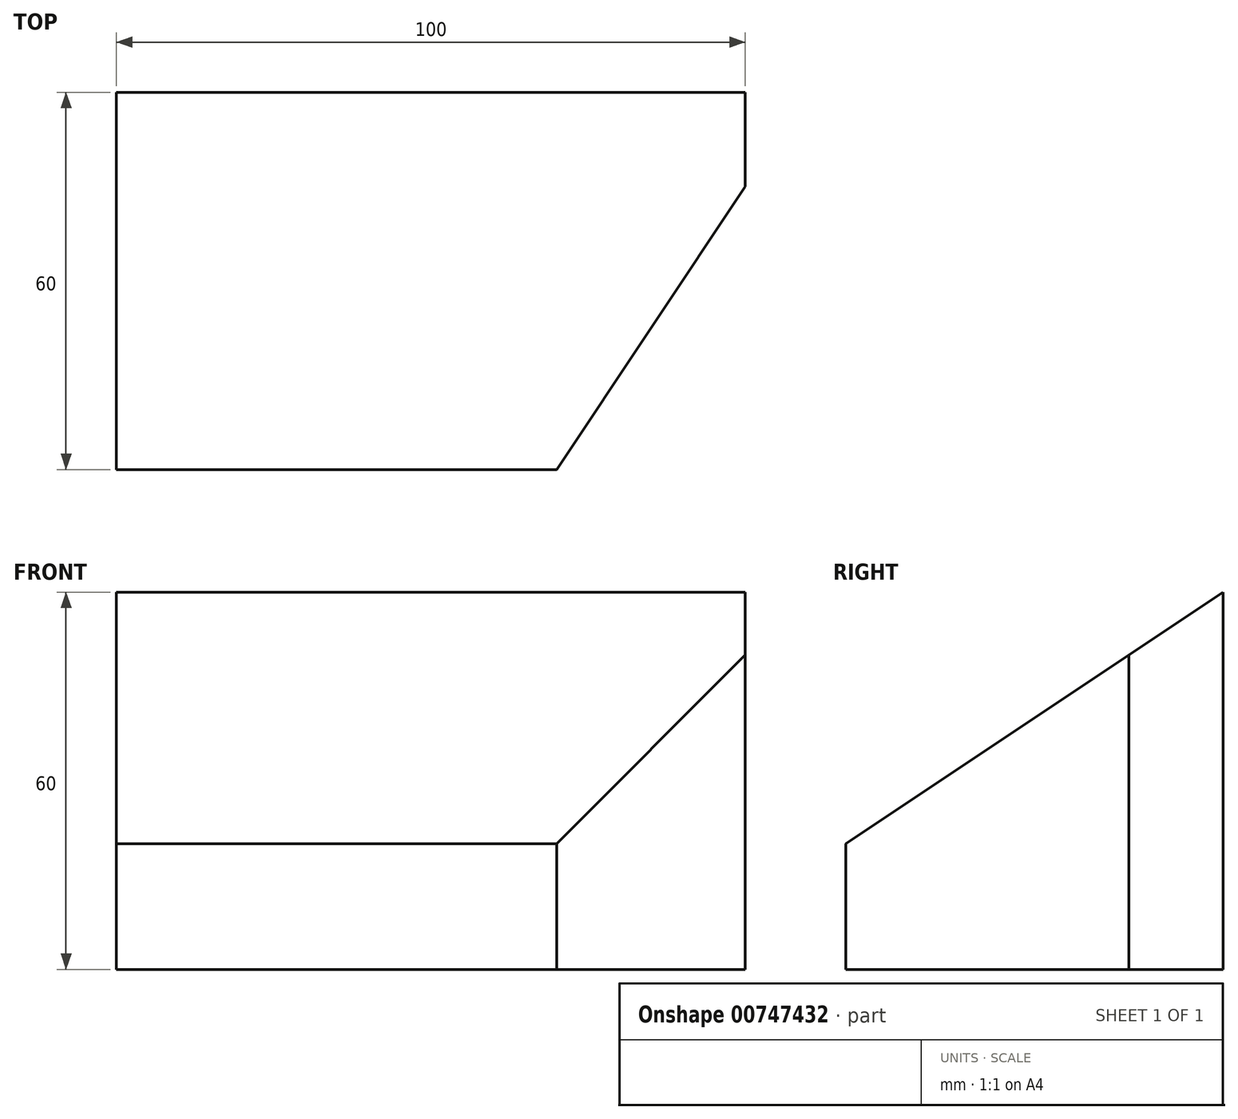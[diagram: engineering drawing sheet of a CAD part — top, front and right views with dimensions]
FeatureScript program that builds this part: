
annotation { "Feature Type Name" : "Feature", "Feature Type Description" : "" }
export const myFeature = defineFeature(function(context is Context, id is Id, definition is map)
    precondition{}
    {
        {
            var Q0;
            Q0=qCreatedBy(makeId("Front.planeOp"),FACE);
            var sketch = newSketch(context, id + "F0", { "sketchPlane" : qUnion([Q0])});
            skLineSegment(sketch, "E0.bottom", {"start": v(0, 0) * mm, "end": v(100, 0) * mm});
            skLineSegment(sketch, "E0.top", {"start": v(0, 60) * mm, "end": v(100, 60) * mm});
            skLineSegment(sketch, "E0.left", {"start": v(0, 0) * mm, "end": v(0, 60) * mm});
            skLineSegment(sketch, "E0.right", {"start": v(100, 0) * mm, "end": v(100, 60) * mm});
            skSolve(sketch);
        }
        {
            var Q0;
            Q0 = qSketchRegion(id + "F0", true);
            extrude(context, id + "F1", {"entities" : qUnion([Q0]), "depth" : 60 * mm, "offsetDistance" : 25 * mm});
        }
        {
            var Q0;
            Q0=makeQuery(id+"F1.opExtrude","SWEPT_FACE",FACE,{"disambiguationData":[OSD([sQuery(id+"F0.wireOp",EDGE,"E0.top")])]});
            var sketch = newSketch(context, id + "F2", { "sketchPlane" : qUnion([Q0])});
            skLineSegment(sketch, "E1", {"start": v(70, -60) * mm, "end": v(100, -15) * mm});
            skSolve(sketch);
        }
        {
            var Q0;
            {var subQ0=sQuery(id+"F2.wireOp",EDGE,"E1");Q0=makeQuery(id+"F2.imprint","IMPRINT",FACE,{"disambiguationData":[TD([[makeQuery(id+"F2.imprint","IMPRINT",EDGE,{"derivedFrom":subQ0}),-1.0]])]});}
            extrude(context, id + "F3", {"entities" : qUnion([Q0]), "operationType" : NewBodyOperationType.REMOVE, "endBound" : BoundingType.THROUGH_ALL, "oppositeDirection" : true, "depth" : 25 * mm, "offsetDistance" : 25 * mm});
        }
        {
            var Q0;
            Q0=makeQuery(id+"F1.opExtrude","SWEPT_FACE",FACE,{"disambiguationData":[OSD([sQuery(id+"F0.wireOp",EDGE,"E0.left")])]});
            var sketch = newSketch(context, id + "F4", { "sketchPlane" : qUnion([Q0])});
            skLineSegment(sketch, "E2", {"start": v(0, 60) * mm, "end": v(60, 20) * mm});
            skSolve(sketch);
        }
        {
            var Q0;
            {var subQ0=sQuery(id+"F4.wireOp",EDGE,"E2");Q0=makeQuery(id+"F4.imprint","IMPRINT",FACE,{"disambiguationData":[TD([[makeQuery(id+"F4.imprint","IMPRINT",EDGE,{"derivedFrom":subQ0}),1.0]])]});}
            extrude(context, id + "F5", {"entities" : qUnion([Q0]), "operationType" : NewBodyOperationType.REMOVE, "endBound" : BoundingType.THROUGH_ALL, "oppositeDirection" : true, "depth" : 25 * mm, "offsetDistance" : 25 * mm});
        }
    });
